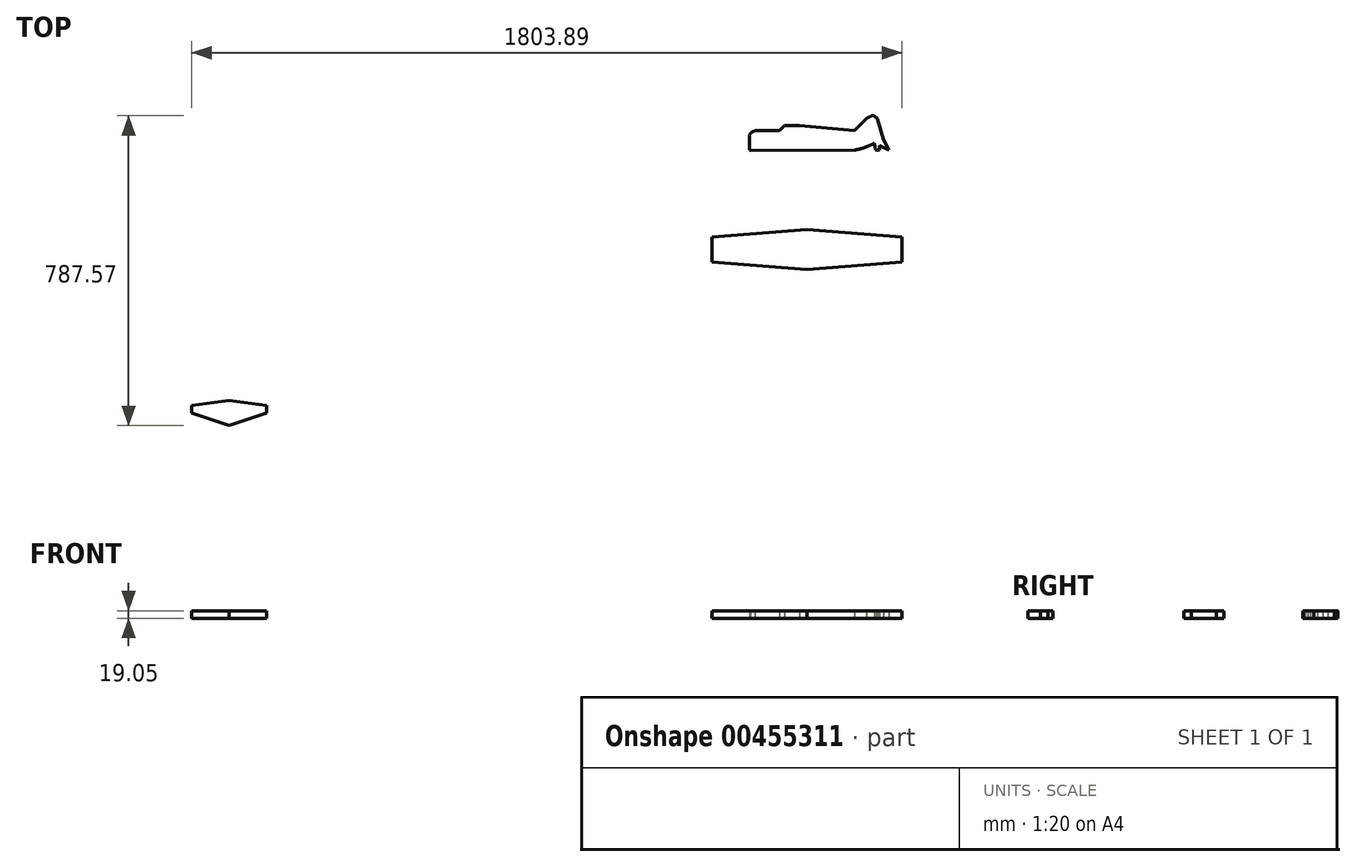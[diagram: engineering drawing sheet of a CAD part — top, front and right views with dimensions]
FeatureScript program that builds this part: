
annotation { "Feature Type Name" : "Feature", "Feature Type Description" : "" }
export const myFeature = defineFeature(function(context is Context, id is Id, definition is map)
    precondition{}
    {
        {
            var Q0;
            Q0=qCreatedBy(makeId("Top.planeOp"),FACE);
            var sketch = newSketch(context, id + "F0", { "sketchPlane" : qUnion([Q0])});
            skLineSegment(sketch, "E0.bottom", {"start": v(-177.8, -50.82) * mm, "end": v(5.78, -49.8) * mm});
            skLineSegment(sketch, "E0.left", {"start": v(-177.8, -44.04) * mm, "end": v(-177.8, -13.35) * mm});
            skPoint(sketch, "E0.middle", {"position": v(0, 0) * mm});
            skLineSegment(sketch, "E1", {"start": v(-177.8, -50.82) * mm, "end": v(-101.6, -50.4) * mm});
            skLineSegment(sketch, "E2", {"start": v(-101.6, 0) * mm, "end": v(-163.67, 0) * mm});
            skLineSegment(sketch, "E3", {"start": v(-177.8, -50.82) * mm, "end": v(-88.9, -50.33) * mm});
            skLineSegment(sketch, "E4", {"start": v(-177.8, -50.82) * mm, "end": v(-50.8, -50.12) * mm});
            skLineSegment(sketch, "E5", {"start": v(-177.8, -50.82) * mm, "end": v(0, -49.84) * mm});
            skLineSegment(sketch, "E6", {"start": v(-177.8, -50.82) * mm, "end": v(88.9, -49.35) * mm});
            skLineSegment(sketch, "E7", {"start": v(-174.34, -50.8) * mm, "end": v(88.9, -49.35) * mm});
            skLineSegment(sketch, "E8", {"start": v(152.4, -49) * mm, "end": v(152.4, -38.1) * mm});
            skLineSegment(sketch, "E9", {"start": v(-163.67, 0) * mm, "end": v(-101.6, 0) * mm});
            skLineSegment(sketch, "E10", {"start": v(-101.6, 0) * mm, "end": v(-88.9, 12.7) * mm});
            skLineSegment(sketch, "E11", {"start": v(-88.9, 12.7) * mm, "end": v(-50.8, 12.7) * mm});
            skLineSegment(sketch, "E12", {"start": v(-50.8, 12.7) * mm, "end": v(88.9, 0) * mm});
            skLineSegment(sketch, "E13", {"start": v(88.9, 0) * mm, "end": v(119.55, 30.65) * mm});
            skLineSegment(sketch, "E14", {"start": v(176.77, -48.87) * mm, "end": v(152.4, -38.1) * mm});
            skLineSegment(sketch, "E15", {"start": v(142.5, -49.05) * mm, "end": v(139.7, -31.75) * mm});
            skFitSpline(sketch, "E16", {"points": [v(139.7, -31.75) * mm, v(88.9, -49.35) * mm, v(5.78, -49.8) * mm], "startDerivative": vector(-105.5, -52.15) * mm, "endDerivative": vector(-160.39, 11.79) * mm});
            skLineSegment(sketch, "E17", {"start": v(148.12, 29.91) * mm, "end": v(162.99, -22.86) * mm});
            skLineSegment(sketch, "E18", {"start": v(162.99, -22.86) * mm, "end": v(176.77, -48.87) * mm});
            skFitSpline(sketch, "E19", {"points": [v(-177.8, -13.35) * mm, v(-174.01, -5.67) * mm, v(-163.67, 0) * mm], "startDerivative": vector(5.73, 18.1) * mm, "endDerivative": vector(22.1, 8.84) * mm});
            skFitSpline(sketch, "E20", {"points": [v(-177.8, -44.04) * mm, v(-174.34, -50.8) * mm, v(-163.33, -50.74) * mm], "startDerivative": vector(4.78, -18.27) * mm, "endDerivative": vector(23.58, 4.07) * mm});
            skPoint(sketch, "E21.1.internal.snap0", {"position": v(136.45, 37.93) * mm});
            skFitSpline(sketch, "E21", {"points": [v(119.55, 30.65) * mm, v(136.45, 38.1) * mm, v(148.12, 29.91) * mm], "startDerivative": vector(33.56, 22.38) * mm, "endDerivative": vector(23.35, -24.87) * mm});
            skLineSegment(sketch, "E22.trimOffspring", {"start": v(142.5, -49.05) * mm, "end": v(152.4, -49) * mm});
            skSolve(sketch);
        }
        {
            var Q0;
            Q0=qCreatedBy(makeId("Top.planeOp"),FACE);
            var sketch = newSketch(context, id + "F1", { "sketchPlane" : qUnion([Q0])});
            skLineSegment(sketch, "E23.left", {"start": v(-273.2, -270.62) * mm, "end": v(-273.2, -334.12) * mm});
            skLineSegment(sketch, "E23.right", {"start": v(209.4, -270.62) * mm, "end": v(209.4, -334.12) * mm});
            skPoint(sketch, "E24.endSnap0", {"position": v(-31.9, -353.17) * mm});
            skLineSegment(sketch, "E25", {"start": v(-273.2, -270.62) * mm, "end": v(-31.9, -251.57) * mm});
            skLineSegment(sketch, "E26", {"start": v(-273.2, -334.12) * mm, "end": v(-31.9, -353.17) * mm});
            skLineSegment(sketch, "E27", {"start": v(209.4, -270.62) * mm, "end": v(-31.9, -251.57) * mm});
            skLineSegment(sketch, "E28", {"start": v(209.4, -334.12) * mm, "end": v(-31.9, -353.17) * mm});
            skSolve(sketch);
        }
        {
            var Q0;
            Q0=qCreatedBy(makeId("Top.planeOp"),FACE);
            var sketch = newSketch(context, id + "F2", { "sketchPlane" : qUnion([Q0])});
            skLineSegment(sketch, "E29.left", {"start": v(-1594.5, -698.63) * mm, "end": v(-1594.5, -717.68) * mm});
            skLineSegment(sketch, "E29.right", {"start": v(-1404, -698.63) * mm, "end": v(-1404, -717.68) * mm});
            skLineSegment(sketch, "E30.top", {"start": v(-1404, -717.68) * mm, "end": v(-1404, -717.68) * mm});
            skLineSegment(sketch, "E31", {"start": v(-1499.25, -685.93) * mm, "end": v(-1404, -698.63) * mm});
            skLineSegment(sketch, "E32", {"start": v(-1499.25, -749.43) * mm, "end": v(-1404, -717.68) * mm});
            skLineSegment(sketch, "E33", {"start": v(-1594.5, -717.68) * mm, "end": v(-1499.25, -749.43) * mm});
            skLineSegment(sketch, "E34", {"start": v(-1594.5, -698.63) * mm, "end": v(-1499.25, -685.93) * mm});
            skSolve(sketch);
        }
        {
            var Q0;
            {var subQ1=sQuery(id+"F0.wireOp",EDGE,"E8");Q0=makeQuery(id+"F0.imprint","IMPRINT",FACE,{"disambiguationData":[TD([[makeQuery(id+"F0.imprint","IMPRINT",EDGE,{"derivedFrom":subQ1}),1.0]])]});}
            extrude(context, id + "F3", {"entities" : qUnion([Q0]), "depth" : 19.05 * mm});
        }
        {
            var Q0;
            Q0=makeQuery(id+"F1.imprint","IMPRINT",FACE,{"disambiguationData":[TD([[makeQuery(id+"F1.imprint","IMPRINT",EDGE,{"derivedFrom":sQuery(id+"F1.wireOp",EDGE,"E23.left")}),1.0]])]});
            extrude(context, id + "F4", {"entities" : qUnion([Q0]), "depth" : 19.05 * mm});
        }
        {
            var Q0;
            Q0=makeQuery(id+"F2.imprint","IMPRINT",FACE,{"disambiguationData":[TD([[makeQuery(id+"F2.imprint","IMPRINT",EDGE,{"derivedFrom":sQuery(id+"F2.wireOp",EDGE,"E29.left")}),1.0]])]});
            extrude(context, id + "F5", {"entities" : qUnion([Q0]), "depth" : 19.05 * mm});
        }
    });
